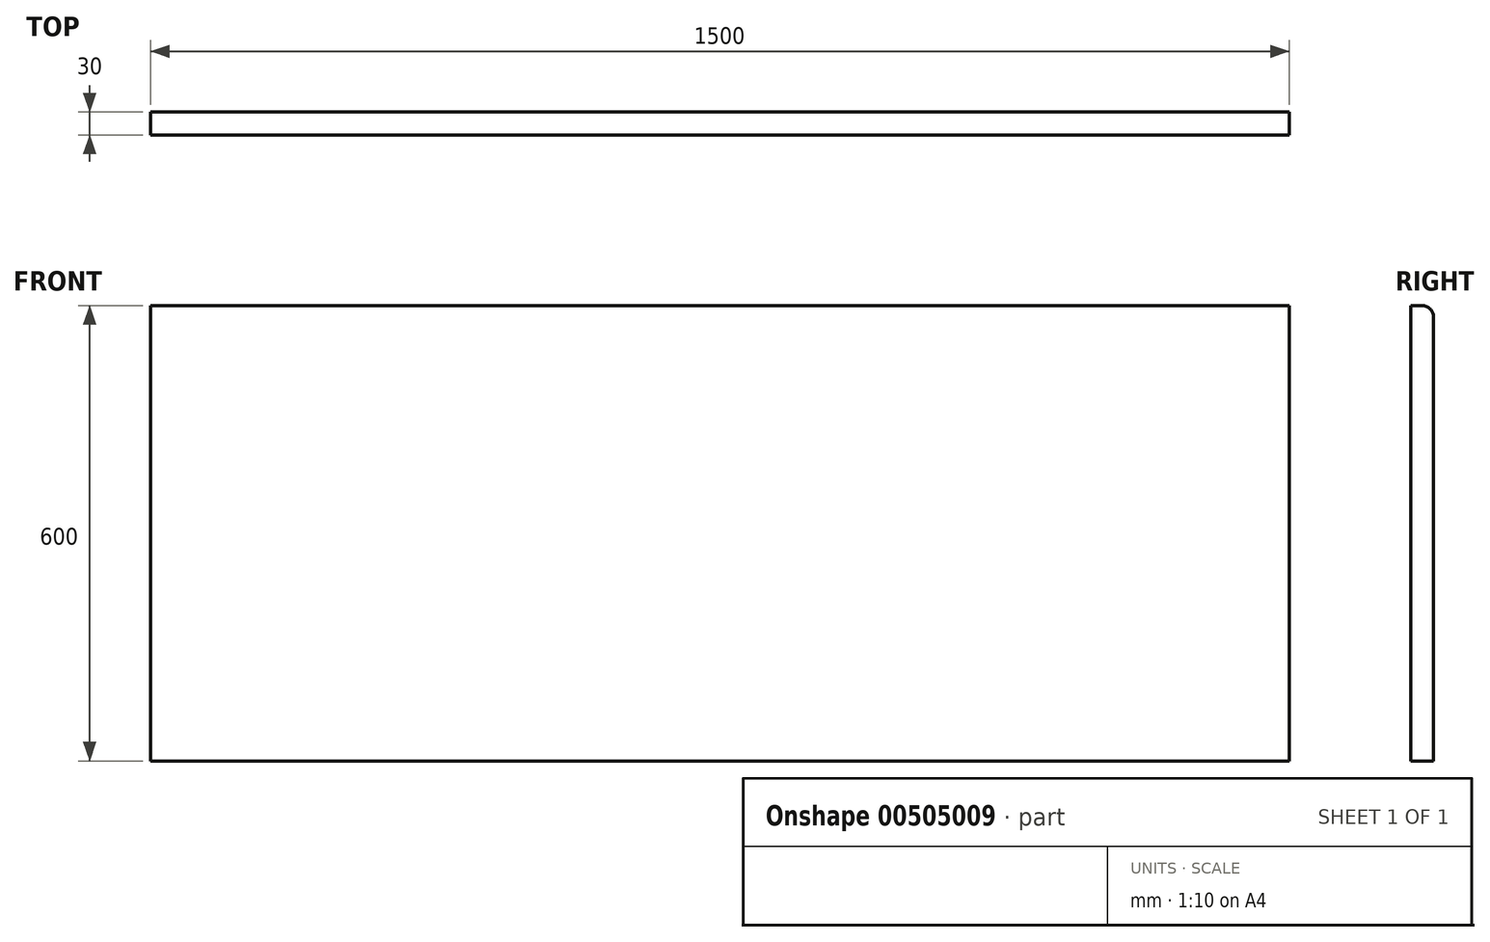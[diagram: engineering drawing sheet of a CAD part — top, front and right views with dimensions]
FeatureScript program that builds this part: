
annotation { "Feature Type Name" : "Feature", "Feature Type Description" : "" }
export const myFeature = defineFeature(function(context is Context, id is Id, definition is map)
    precondition{}
    {
        {
            var Q0;
            Q0=qCreatedBy(makeId("Front.planeOp"),FACE);
            var sketch = newSketch(context, id + "F0", { "sketchPlane" : qUnion([Q0])});
            skLineSegment(sketch, "E0.bottom", {"start": v(-750, 0) * mm, "end": v(750, 0) * mm});
            skLineSegment(sketch, "E0.top", {"start": v(-750, -600) * mm, "end": v(750, -600) * mm});
            skLineSegment(sketch, "E0.left", {"start": v(-750, 0) * mm, "end": v(-750, -600) * mm});
            skLineSegment(sketch, "E0.right", {"start": v(750, 0) * mm, "end": v(750, -600) * mm});
            skSolve(sketch);
        }
        {
            var Q0;
            Q0=qSketchRegion(id+"F0",true);
            extrude(context, id + "F1", {"entities" : qUnion([Q0]), "depth" : 30 * mm});
        }
        {
            var Q0;
            Q0=makeQuery(id+"F1.opExtrude","CAP_EDGE",EDGE,{"disambiguationData":[OSD([sQuery(id+"F0.wireOp",EDGE,"E0.bottom")])],"isStart":true});
            fillet(context, id + "F2", {"entities" : qUnion([Q0]), "radius" : 15 * mm, "tangentPropagation" : true, "allowEdgeOverflow" : false});
        }
    });
